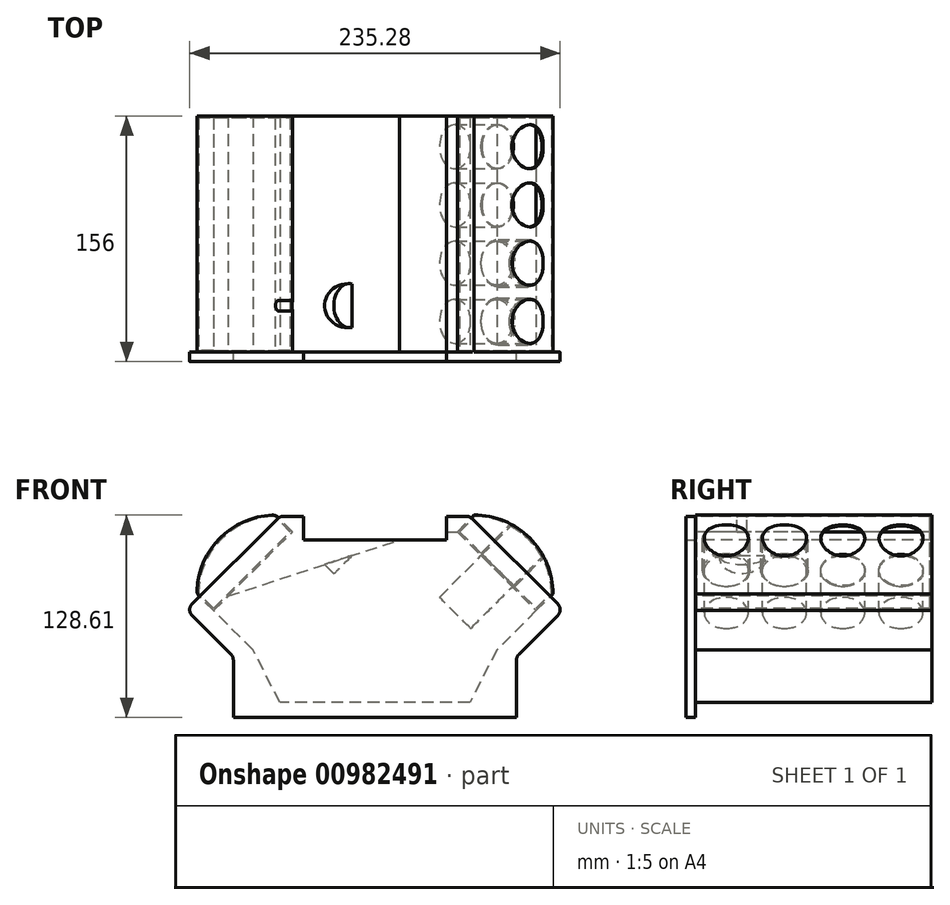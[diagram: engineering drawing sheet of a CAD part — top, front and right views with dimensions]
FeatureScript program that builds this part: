
annotation { "Feature Type Name" : "Feature", "Feature Type Description" : "" }
export const myFeature = defineFeature(function(context is Context, id is Id, definition is map)
    precondition{}
    {
        {
            var Q0;
            Q0=qCreatedBy(makeId("Front.planeOp"),FACE);
            var sketch = newSketch(context, id + "F0", { "sketchPlane" : qUnion([Q0])});
            skLineSegment(sketch, "E0.MirrorCS", {"start": v(89.95, -18.6) * mm, "end": v(70, -57.31) * mm});
            skLineSegment(sketch, "E1", {"start": v(119.71, 11.17) * mm, "end": v(89.95, -18.6) * mm});
            skLineSegment(sketch, "E2", {"start": v(119.71, 11.17) * mm, "end": v(60.48, 70.4) * mm});
            skLineSegment(sketch, "E3", {"start": v(-119.71, 11.17) * mm, "end": v(-60.48, 70.4) * mm});
            skLineSegment(sketch, "E4", {"start": v(-70, -57.31) * mm, "end": v(-89.95, -18.6) * mm});
            skLineSegment(sketch, "E5", {"start": v(-119.71, 11.17) * mm, "end": v(-89.95, -18.6) * mm});
            skLineSegment(sketch, "E6", {"start": v(-70, -57.31) * mm, "end": v(70, -57.31) * mm});
            skLineSegment(sketch, "E7", {"start": v(-89.95, -18.6) * mm, "end": v(89.95, -18.6) * mm, "construction": true});
            skLineSegment(sketch, "E8", {"start": v(-89.95, -18.6) * mm, "end": v(-89.95, -57.31) * mm});
            skLineSegment(sketch, "E9", {"start": v(-89.95, -57.31) * mm, "end": v(-70, -57.31) * mm});
            skLineSegment(sketch, "E10", {"start": v(89.95, -18.6) * mm, "end": v(89.95, -57.31) * mm});
            skLineSegment(sketch, "E11", {"start": v(89.95, -57.31) * mm, "end": v(70, -57.31) * mm});
            skLineSegment(sketch, "E12", {"start": v(-60.48, 70.4) * mm, "end": v(-45.48, 70.4) * mm});
            skLineSegment(sketch, "E13", {"start": v(-45.48, 70.4) * mm, "end": v(-45.48, 55.4) * mm});
            skLineSegment(sketch, "E14", {"start": v(60.48, 70.4) * mm, "end": v(45.48, 70.4) * mm});
            skLineSegment(sketch, "E15", {"start": v(45.48, 70.4) * mm, "end": v(45.48, 55.4) * mm});
            skLineSegment(sketch, "E16", {"start": v(45.48, 55.4) * mm, "end": v(-45.48, 55.4) * mm});
            skSolve(sketch);
        }
        {
            var Q0;
            Q0 = qSketchRegion(id + "F0", true);
            extrude(context, id + "F1", {"entities" : qUnion([Q0]), "depth" : 6 * mm, "offsetDistance" : 25 * mm});
        }
        {
            var Q0;
            Q0=makeQuery(id+"F1.opExtrude","CAP_FACE",FACE,{"disambiguationData":[OSD([sQuery(id+"F0.wireOp",EDGE,"E0.MirrorCS"),sQuery(id+"F0.wireOp",EDGE,"E1"),sQuery(id+"F0.wireOp",EDGE,"E2"),sQuery(id+"F0.wireOp",EDGE,"m8CZ9T74-qpoT-QNDn-k5fx-l1FQIkovVV6P"),sQuery(id+"F0.wireOp",EDGE,"E3"),sQuery(id+"F0.wireOp",EDGE,"E4"),sQuery(id+"F0.wireOp",EDGE,"E5"),sQuery(id+"F0.wireOp",EDGE,"E6")])],"isStart":true});
            var sketch = newSketch(context, id + "F2", { "sketchPlane" : qUnion([Q0])});
            skLineSegment(sketch, "E17.0.0", {"start": v(61.56, -57.31) * mm, "end": v(86.05, -22.5) * mm});
            skLineSegment(sketch, "E17.0.1", {"start": v(86.05, -22.5) * mm, "end": v(119.71, 11.17) * mm});
            skLineSegment(sketch, "E17.0.2", {"start": v(119.71, 11.17) * mm, "end": v(119.71, 11.17) * mm});
            skLineSegment(sketch, "E17.0.3", {"start": v(119.71, 11.17) * mm, "end": v(-60.68, 70.2) * mm});
            skLineSegment(sketch, "E17.0.4", {"start": v(-60.68, 70.2) * mm, "end": v(-119.71, 11.17) * mm});
            skLineSegment(sketch, "E17.0.5", {"start": v(-119.71, 11.17) * mm, "end": v(-89.95, -18.6) * mm});
            skLineSegment(sketch, "E17.0.6", {"start": v(-89.95, -18.6) * mm, "end": v(-61.56, -57.31) * mm});
            skLineSegment(sketch, "E17.0.7", {"start": v(-61.56, -57.31) * mm, "end": v(61.56, -57.31) * mm});
            skLineSegment(sketch, "E18.0", {"start": v(-60.34, -47.61) * mm, "end": v(60.34, -47.61) * mm});
            skLineSegment(sketch, "E18.1", {"start": v(-77.47, -14.37) * mm, "end": v(-60.34, -47.61) * mm});
            skLineSegment(sketch, "E18.2", {"start": v(60.34, -47.61) * mm, "end": v(77.47, -14.37) * mm});
            skLineSegment(sketch, "E18.3", {"start": v(-102.45, 10.6) * mm, "end": v(-77.47, -14.37) * mm});
            skLineSegment(sketch, "E18.4", {"start": v(77.47, -14.37) * mm, "end": v(102.45, 10.6) * mm});
            skLineSegment(sketch, "E18.5", {"start": v(102.45, 10.6) * mm, "end": v(52.36, 60.7) * mm});
            skLineSegment(sketch, "E18.6", {"start": v(52.36, 60.7) * mm, "end": v(-52.36, 60.7) * mm});
            skLineSegment(sketch, "E18.7", {"start": v(-52.36, 60.7) * mm, "end": v(-102.45, 10.6) * mm});
            skSolve(sketch);
        }
        {
            var Q0;
            Q0=makeQuery(id+"F2.imprint","IMPRINT",FACE,{"disambiguationData":[TD([[makeQuery(id+"F2.imprint","IMPRINT",EDGE,{"derivedFrom":sQuery(id+"F2.wireOp",EDGE,"E18.0")}),1.0]])]});
            extrude(context, id + "F3", {"entities" : qUnion([Q0]), "depth" : 150 * mm, "offsetDistance" : 25 * mm});
        }
        {
            var Q0;
            Q0=makeQuery(id+"F3.opExtrude","SWEPT_FACE",FACE,{"disambiguationData":[OSD([sQuery(id+"F2.wireOp",EDGE,"E18.7")])]});
            var Q1;
            Q1=makeQuery(id+"F3.opExtrude","SWEPT_FACE",FACE,{"disambiguationData":[OSD([sQuery(id+"F2.wireOp",EDGE,"E18.7")])]});
            var sketch = newSketch(context, id + "F4", { "sketchPlane" : qUnion([Q0, Q1])});
            skSolve(sketch);
        }
        {
            var Q0;
            {var subQ0=sQuery(id+"F2.wireOp",EDGE,"E18.7");Q0=makeQuery(id+"F4.imprint","IMPRINT",FACE,{"disambiguationData":[TD([[makeQuery(id+"F4.imprint","IMPRINT",EDGE,{"derivedFrom":makeQuery(id+"F3.opExtrude","CAP_EDGE",EDGE,{"disambiguationData":[OSD([subQ0])],"isStart":true})}),1.0]])]});}
            var sketch = newSketch(context, id + "F5", { "sketchPlane" : qUnion([Q0])});
            skLineSegment(sketch, "E19.0.0", {"start": v(150, 5.9) * mm, "end": v(0, 5.9) * mm, "construction": true});
            skLineSegment(sketch, "E19.0.1", {"start": v(0, 5.9) * mm, "end": v(0, -64.94) * mm, "construction": true});
            skLineSegment(sketch, "E19.0.2", {"start": v(0, -64.94) * mm, "end": v(150, -64.94) * mm, "construction": true});
            skLineSegment(sketch, "E19.0.3", {"start": v(150, -64.94) * mm, "end": v(150, 5.9) * mm, "construction": true});
            skLineSegment(sketch, "E20", {"start": v(19.15, 5.9) * mm, "end": v(19.15, -29.5) * mm, "construction": true});
            skCircle(sketch, "E21", {"center": v(19.5, -29.5) * mm, "radius": 14 * mm});
            skLineSegment(sketch, "E22", {"start": v(19.5, -29.5) * mm, "end": v(56.5, -29.5) * mm, "construction": true});
            skCircle(sketch, "E23", {"center": v(56.5, -29.5) * mm, "radius": 14 * mm});
            skLineSegment(sketch, "E24", {"start": v(56.5, -29.5) * mm, "end": v(93.5, -29.5) * mm, "construction": true});
            skCircle(sketch, "E25", {"center": v(93.5, -29.5) * mm, "radius": 14 * mm});
            skLineSegment(sketch, "E26", {"start": v(93.5, -29.5) * mm, "end": v(130.5, -29.5) * mm, "construction": true});
            skCircle(sketch, "E27", {"center": v(130.5, -29.5) * mm, "radius": 14 * mm});
            skSolve(sketch);
        }
        {
            var Q0;
            Q0=makeQuery(id+"F1.opExtrude","CAP_FACE",FACE,{"disambiguationData":[OSD([sQuery(id+"F0.wireOp",EDGE,"E0.MirrorCS"),sQuery(id+"F0.wireOp",EDGE,"E1"),sQuery(id+"F0.wireOp",EDGE,"E2"),sQuery(id+"F0.wireOp",EDGE,"m8CZ9T74-qpoT-QNDn-k5fx-l1FQIkovVV6P"),sQuery(id+"F0.wireOp",EDGE,"E3"),sQuery(id+"F0.wireOp",EDGE,"E4"),sQuery(id+"F0.wireOp",EDGE,"E5"),sQuery(id+"F0.wireOp",EDGE,"E6")])],"isStart":true});
            var sketch = newSketch(context, id + "F6", { "sketchPlane" : qUnion([Q0])});
            skLineSegment(sketch, "E28.0", {"start": v(-52.36, 60.7) * mm, "end": v(-102.45, 10.6) * mm});
            skLineSegment(sketch, "E29", {"start": v(-102.45, 10.6) * mm, "end": v(-113.05, 21.22) * mm});
            skLineSegment(sketch, "E30", {"start": v(-52.36, 60.7) * mm, "end": v(-62.96, 71.3) * mm});
            skArc(sketch, "E31", {"start": v(-62.96, 71.3) * mm, "mid": v(-98.4, 56.66) * mm, "end": v(-113.05, 21.22) * mm});
            skSolve(sketch);
        }
        {
            var Q0;
            {var subQ0=sQuery(id+"F6.wireOp",EDGE,"E28.0");Q0=makeQuery(id+"F6.imprint","IMPRINT",FACE,{"disambiguationData":[TD([[makeQuery(id+"F6.imprint","IMPRINT",EDGE,{"derivedFrom":subQ0}),-1.0]])]});}
            var Q1;
            {var subQ0=sQuery(id+"F6.wireOp",EDGE,"E31");Q1=makeQuery(id+"F6.imprint","IMPRINT",FACE,{"disambiguationData":[TD([[makeQuery(id+"F6.imprint","IMPRINT",EDGE,{"derivedFrom":subQ0}),1.0]])]});}
            extrude(context, id + "F7", {"entities" : qUnion([Q0, Q1]), "depth" : 150 * mm, "offsetDistance" : 25 * mm});
        }
        {
            var Q0;
            Q0 = qSketchRegion(id + "F5", true);
            var Q1;
            Q1 = qConstructionFilter(qBodyType(qCreatedBy(id + "F6" ,EDGE), BodyType.WIRE), ConstructionObject.NO);
            extrude(context, id + "F8", {"entities" : qUnion([Q0]), "operationType" : NewBodyOperationType.REMOVE, "surfaceEntities" : qUnion([Q1]), "endBound" : BoundingType.SYMMETRIC, "oppositeDirection" : true, "depth" : 75 * mm, "offsetDistance" : 25 * mm});
        }
        {
            var Q0;
            Q0=makeQuery(id+"F3.opExtrude","SWEPT_FACE",FACE,{"disambiguationData":[OSD([sQuery(id+"F2.wireOp",EDGE,"E18.5")])]});
            var sketch = newSketch(context, id + "F9", { "sketchPlane" : qUnion([Q0])});
            skLineSegment(sketch, "E32.0", {"start": v(5.9, 150) * mm, "end": v(5.9, 0) * mm, "construction": true});
            skLineSegment(sketch, "E33.0", {"start": v(-64.94, 0) * mm, "end": v(5.9, 0) * mm, "construction": true});
            skLineSegment(sketch, "E34", {"start": v(5.9, 89.45) * mm, "end": v(-29.5, 89.45) * mm, "construction": true});
            skLineSegment(sketch, "E35", {"start": v(-29.5, 89.45) * mm, "end": v(-29.5, 0) * mm, "construction": true});
            skLineSegment(sketch, "E36", {"start": v(-29.5, 0) * mm, "end": v(-29.5, 19.5) * mm, "construction": true});
            skCircle(sketch, "E37", {"center": v(-29.5, 19.5) * mm, "radius": 14 * mm});
            skCircle(sketch, "E38.0.1.0", {"center": v(-29.5, 56.5) * mm, "radius": 14 * mm});
            skCircle(sketch, "E38.0.2.0", {"center": v(-29.5, 93.5) * mm, "radius": 14 * mm});
            skCircle(sketch, "E38.0.3.0", {"center": v(-29.5, 130.5) * mm, "radius": 14 * mm});
            skLineSegment(sketch, "E38.direction1", {"start": v(-29.5, 19.5) * mm, "end": v(-4.5, 19.5) * mm, "construction": true});
            skLineSegment(sketch, "E38.direction2", {"start": v(-29.5, 19.5) * mm, "end": v(-29.5, 56.5) * mm, "construction": true});
            skSolve(sketch);
        }
        {
            var Q0;
            Q0=makeQuery(id+"F1.opExtrude","CAP_FACE",FACE,{"disambiguationData":[OSD([sQuery(id+"F0.wireOp",EDGE,"E0.MirrorCS"),sQuery(id+"F0.wireOp",EDGE,"E1"),sQuery(id+"F0.wireOp",EDGE,"E2"),sQuery(id+"F0.wireOp",EDGE,"m8CZ9T74-qpoT-QNDn-k5fx-l1FQIkovVV6P"),sQuery(id+"F0.wireOp",EDGE,"E3"),sQuery(id+"F0.wireOp",EDGE,"E4"),sQuery(id+"F0.wireOp",EDGE,"E5"),sQuery(id+"F0.wireOp",EDGE,"E6")])],"isStart":true});
            var sketch = newSketch(context, id + "F10", { "sketchPlane" : qUnion([Q0])});
            skLineSegment(sketch, "E39.0", {"start": v(102.45, 10.6) * mm, "end": v(52.36, 60.7) * mm});
            skLineSegment(sketch, "E40", {"start": v(52.36, 60.7) * mm, "end": v(62.96, 71.3) * mm});
            skLineSegment(sketch, "E41", {"start": v(102.45, 10.6) * mm, "end": v(113.05, 21.22) * mm});
            skArc(sketch, "E42", {"start": v(113.05, 21.22) * mm, "mid": v(98.4, 56.66) * mm, "end": v(62.96, 71.3) * mm});
            skSolve(sketch);
        }
        {
            var Q0;
            {var subQ0=sQuery(id+"F10.wireOp",EDGE,"E39.0");Q0=makeQuery(id+"F10.imprint","IMPRINT",FACE,{"disambiguationData":[TD([[makeQuery(id+"F10.imprint","IMPRINT",EDGE,{"derivedFrom":subQ0}),-1.0]])]});}
            var Q1;
            {var subQ0=sQuery(id+"F10.wireOp",EDGE,"E42");Q1=makeQuery(id+"F10.imprint","IMPRINT",FACE,{"disambiguationData":[TD([[makeQuery(id+"F10.imprint","IMPRINT",EDGE,{"derivedFrom":subQ0}),1.0]])]});}
            extrude(context, id + "F11", {"entities" : qUnion([Q0, Q1]), "depth" : 150 * mm, "offsetDistance" : 25 * mm});
        }
        {
            var Q0;
            Q0 = qSketchRegion(id + "F9", true);
            extrude(context, id + "F12", {"entities" : qUnion([Q0]), "operationType" : NewBodyOperationType.REMOVE, "endBound" : BoundingType.SYMMETRIC, "oppositeDirection" : true, "depth" : 75 * mm, "offsetDistance" : 25 * mm});
        }
        {
            var Q0;
            Q0=makeQuery(id+"F3.opExtrude","CAP_FACE",FACE,{"disambiguationData":[OSD([sQuery(id+"F2.wireOp",EDGE,"E18.0"),sQuery(id+"F2.wireOp",EDGE,"E18.1"),sQuery(id+"F2.wireOp",EDGE,"E18.2"),sQuery(id+"F2.wireOp",EDGE,"E18.3"),sQuery(id+"F2.wireOp",EDGE,"E18.4"),sQuery(id+"F2.wireOp",EDGE,"E18.5"),sQuery(id+"F2.wireOp",EDGE,"E18.6"),sQuery(id+"F2.wireOp",EDGE,"E18.7")])],"isStart":false});
            var sketch = newSketch(context, id + "F13", { "sketchPlane" : qUnion([Q0])});
            skLineSegment(sketch, "E43.0", {"start": v(-45.48, 60.7) * mm, "end": v(-52.36, 60.7) * mm});
            skLineSegment(sketch, "E44.0", {"start": v(-52.36, 60.7) * mm, "end": v(-102.45, 10.6) * mm});
            skLineSegment(sketch, "E45.0", {"start": v(-102.45, 10.6) * mm, "end": v(-77.47, -14.37) * mm});
            skLineSegment(sketch, "E46.0", {"start": v(-77.47, -14.37) * mm, "end": v(-60.34, -47.61) * mm});
            skLineSegment(sketch, "E47.0", {"start": v(-60.34, -47.61) * mm, "end": v(60.34, -47.61) * mm});
            skLineSegment(sketch, "E48.0", {"start": v(60.34, -47.61) * mm, "end": v(77.47, -14.37) * mm});
            skLineSegment(sketch, "E49.0", {"start": v(77.47, -14.37) * mm, "end": v(102.45, 10.6) * mm});
            skLineSegment(sketch, "E50.0", {"start": v(102.45, 10.6) * mm, "end": v(52.36, 60.7) * mm});
            skLineSegment(sketch, "E51.0", {"start": v(101.03, 10.6) * mm, "end": v(51.94, 59.7) * mm});
            skLineSegment(sketch, "E51.1", {"start": v(76.65, -13.77) * mm, "end": v(101.03, 10.6) * mm});
            skLineSegment(sketch, "E51.2", {"start": v(51.94, 59.7) * mm, "end": v(-51.94, 59.7) * mm});
            skLineSegment(sketch, "E51.3", {"start": v(59.73, -46.61) * mm, "end": v(76.65, -13.77) * mm});
            skLineSegment(sketch, "E51.4", {"start": v(-51.94, 59.7) * mm, "end": v(-101.03, 10.6) * mm});
            skLineSegment(sketch, "E51.5", {"start": v(-101.03, 10.6) * mm, "end": v(-76.65, -13.77) * mm});
            skLineSegment(sketch, "E51.6", {"start": v(-76.65, -13.77) * mm, "end": v(-59.73, -46.61) * mm});
            skLineSegment(sketch, "E51.7", {"start": v(-59.73, -46.61) * mm, "end": v(59.73, -46.61) * mm});
            skSolve(sketch);
        }
        {
            var Q0;
            Q0=makeQuery(id+"F13.imprint","IMPRINT",FACE,{"disambiguationData":[TD([[makeQuery(id+"F13.imprint","IMPRINT",EDGE,{"derivedFrom":sQuery(id+"F13.wireOp",EDGE,"E51.0")}),1.0]])]});
            extrude(context, id + "F14", {"entities" : qUnion([Q0]), "operationType" : NewBodyOperationType.REMOVE, "oppositeDirection" : true, "depth" : 150 * mm, "offsetDistance" : 25 * mm});
        }
        {
            var Q0;
            Q0=makeQuery(id+"F1.opExtrude","SWEPT_EDGE",EDGE,{"disambiguationData":[OSD([sQuery(id+"F0.wireOp",EDGE,"E3"),sQuery(id+"F0.wireOp",EDGE,"E5")])]});
            var Q1;
            Q1=makeQuery(id+"F1.opExtrude","SWEPT_EDGE",EDGE,{"disambiguationData":[OSD([sQuery(id+"F0.wireOp",EDGE,"E4"),sQuery(id+"F0.wireOp",EDGE,"E5")])]});
            var Q2;
            Q2=makeQuery(id+"F1.opExtrude","SWEPT_EDGE",EDGE,{"disambiguationData":[OSD([sQuery(id+"F0.wireOp",EDGE,"E4"),sQuery(id+"F0.wireOp",EDGE,"E6")])]});
            var Q3;
            Q3=makeQuery(id+"F1.opExtrude","SWEPT_EDGE",EDGE,{"disambiguationData":[OSD([sQuery(id+"F0.wireOp",EDGE,"E0.MirrorCS"),sQuery(id+"F0.wireOp",EDGE,"E1")])]});
            var Q4;
            Q4=makeQuery(id+"F1.opExtrude","SWEPT_EDGE",EDGE,{"disambiguationData":[OSD([sQuery(id+"F0.wireOp",EDGE,"E0.MirrorCS"),sQuery(id+"F0.wireOp",EDGE,"E6")])]});
            var Q5;
            Q5=makeQuery(id+"F1.opExtrude","SWEPT_EDGE",EDGE,{"disambiguationData":[OSD([sQuery(id+"F0.wireOp",EDGE,"E1"),sQuery(id+"F0.wireOp",EDGE,"E2")])]});
            var Q6;
            Q6=makeQuery(id+"F1.opExtrude","SWEPT_EDGE",EDGE,{"disambiguationData":[OSD([sQuery(id+"F0.wireOp",EDGE,"E2"),sQuery(id+"F0.wireOp",EDGE,"m8CZ9T74-qpoT-QNDn-k5fx-l1FQIkovVV6P")])]});
            var Q7;
            Q7=makeQuery(id+"F1.opExtrude","SWEPT_EDGE",EDGE,{"disambiguationData":[OSD([sQuery(id+"F0.wireOp",EDGE,"m8CZ9T74-qpoT-QNDn-k5fx-l1FQIkovVV6P"),sQuery(id+"F0.wireOp",EDGE,"E3")])]});
            fillet(context, id + "F15", {"entities" : qUnion([Q0, Q1, Q2, Q3, Q4, Q5, Q6, Q7]), "radius" : 5 * mm, "tangentPropagation" : true, "allowEdgeOverflow" : false});
        }
        {
            var Q0;
            Q0=makeQuery(id+"F12.boolean.opBoolean","COPY",FACE,{"disambiguationData":[TD([makeQuery(id+"F11.opExtrude","SWEPT_FACE",FACE,{"disambiguationData":[OSD([sQuery(id+"F10.wireOp",EDGE,"E39.0")])]})])],"derivedFrom":makeQuery(id+"F12.opExtrude","SWEPT_FACE",FACE,{"disambiguationData":[OSD([sQuery(id+"F9.wireOp",EDGE,"E37")])]})});
            shell(context, id + "F16", {"entities" : qUnion([Q0]), "thickness" : 1 * mm});
        }
        {
            var Q0;
            Q0=makeQuery(id+"F11.opExtrude","SWEPT_EDGE",EDGE,{"disambiguationData":[OSD([sQuery(id+"F10.wireOp",EDGE,"E41"),sQuery(id+"F10.wireOp",EDGE,"E42")])]});
            var Q1;
            Q1=makeQuery(id+"F11.opExtrude","SWEPT_EDGE",EDGE,{"disambiguationData":[OSD([sQuery(id+"F10.wireOp",EDGE,"E40"),sQuery(id+"F10.wireOp",EDGE,"E42")])]});
            fillet(context, id + "F17", {"entities" : qUnion([Q0, Q1]), "radius" : 5 * mm, "tangentPropagation" : true, "allowEdgeOverflow" : false});
        }
        {
            var Q0;
            Q0=makeQuery(id+"F8.boolean.opBoolean","COPY",FACE,{"disambiguationData":[TD([makeQuery(id+"F7.opExtrude","SWEPT_FACE",FACE,{"disambiguationData":[OSD([sQuery(id+"F6.wireOp",EDGE,"E28.0")])]})])],"derivedFrom":makeQuery(id+"F8.opExtrude","SWEPT_FACE",FACE,{"disambiguationData":[OSD([sQuery(id+"F5.wireOp",EDGE,"E25")])]})});
            var Q1;
            Q1=makeQuery(id+"F8.boolean.opBoolean","COPY",FACE,{"disambiguationData":[TD([makeQuery(id+"F7.opExtrude","SWEPT_FACE",FACE,{"disambiguationData":[OSD([sQuery(id+"F6.wireOp",EDGE,"E28.0")])]})])],"derivedFrom":makeQuery(id+"F8.opExtrude","SWEPT_FACE",FACE,{"disambiguationData":[OSD([sQuery(id+"F5.wireOp",EDGE,"E27")])]})});
            shell(context, id + "F18", {"entities" : qUnion([Q0, Q1]), "thickness" : 1 * mm});
        }
    });
